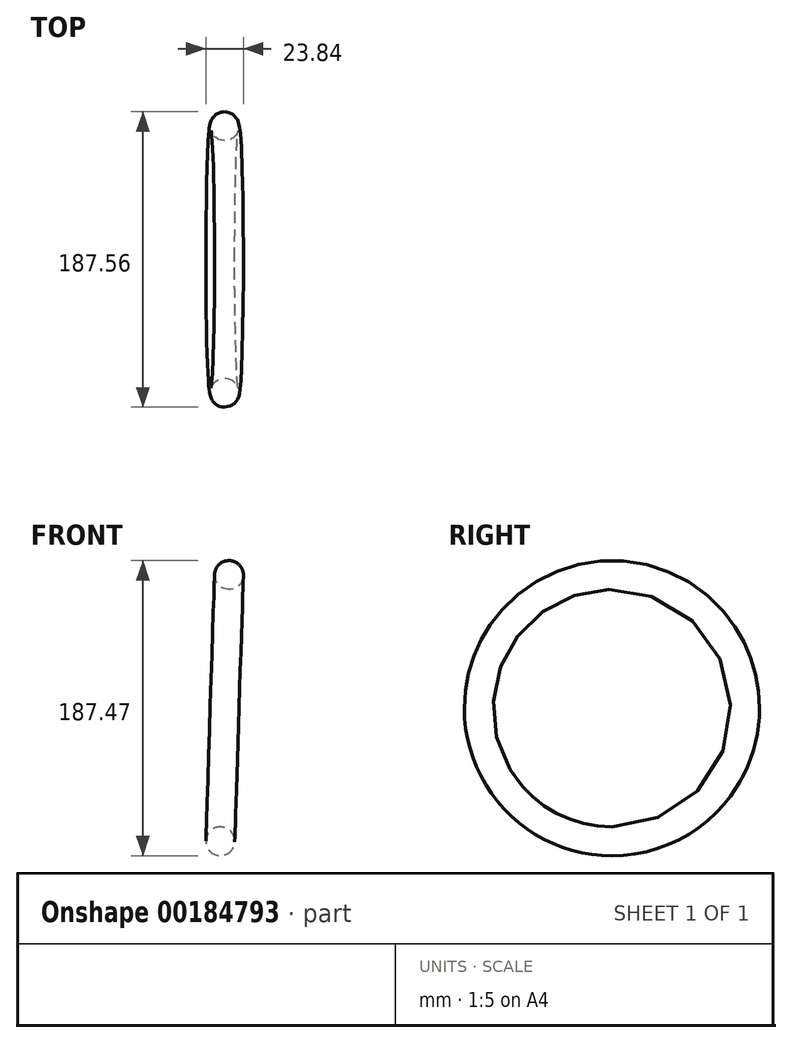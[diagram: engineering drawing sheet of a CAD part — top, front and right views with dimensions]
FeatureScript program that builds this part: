
annotation { "Feature Type Name" : "Feature", "Feature Type Description" : "" }
export const myFeature = defineFeature(function(context is Context, id is Id, definition is map)
    precondition{}
    {
        {
            var Q0;
            Q0=qCreatedBy(makeId("Front.planeOp"),FACE);
            var sketch = newSketch(context, id + "F0", { "sketchPlane" : qUnion([Q0])});
            skCircle(sketch, "E0", {"center": v(-8.63, 84.94) * mm, "radius": 9.17 * mm});
            skSolve(sketch);
        }
        {
            var Q0;
            Q0=qCreatedBy(makeId("Front.planeOp"),FACE);
            var sketch = newSketch(context, id + "F1", { "sketchPlane" : qUnion([Q0])});
            skLineSegment(sketch, "E1", {"start": v(0, 0) * mm, "end": v(112.82, -3.67) * mm});
            skLineSegment(sketch, "E2", {"start": v(0, 0) * mm, "end": v(-121.94, 3.97) * mm});
            skSolve(sketch);
        }
        {
            var Q0;
            Q0 = qSketchRegion(id + "F0", true);
            var Q1;
            Q1=sQuery(id+"F1.wireOp",EDGE,"E2");
            revolve(context, id + "F2", {"entities" : qUnion([Q0]), "axis" : qUnion([Q1]), "revolveType" : RevolveType.FULL});
        }
    });
